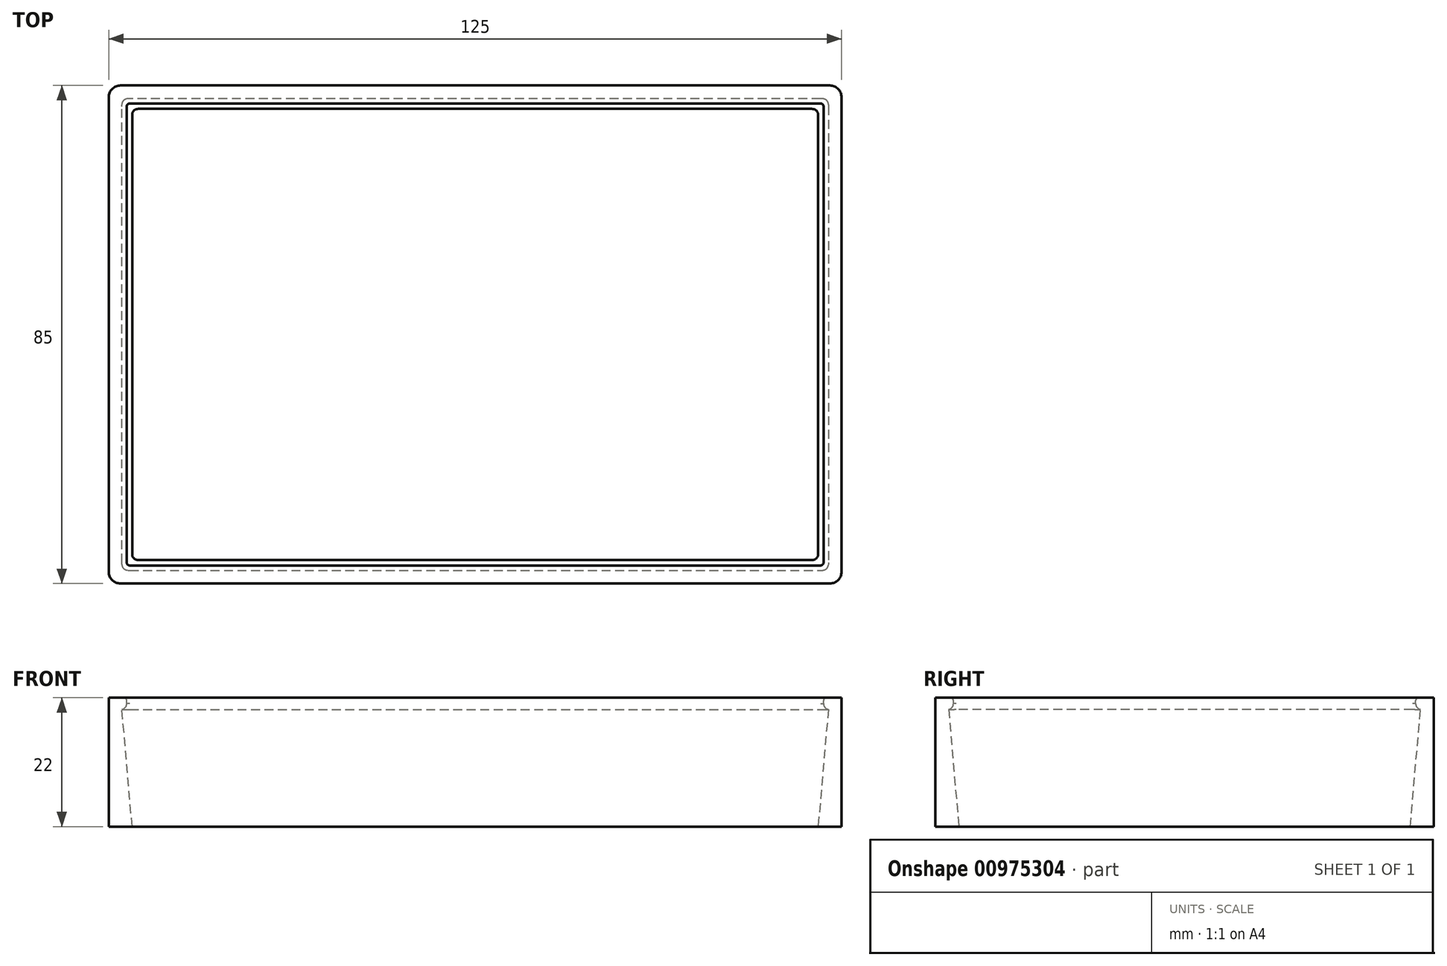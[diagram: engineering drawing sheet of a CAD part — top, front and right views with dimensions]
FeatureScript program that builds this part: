
annotation { "Feature Type Name" : "Feature", "Feature Type Description" : "" }
export const myFeature = defineFeature(function(context is Context, id is Id, definition is map)
    precondition{}
    {
        {
            var Q0;
            Q0=qCreatedBy(makeId("Top.planeOp"),FACE);
            var sketch = newSketch(context, id + "F0", { "sketchPlane" : qUnion([Q0])});
            skLineSegment(sketch, "E0.bottom", {"start": v(-62.5, 42.5) * mm, "end": v(62.5, 42.5) * mm});
            skLineSegment(sketch, "E0.top", {"start": v(-62.5, -42.5) * mm, "end": v(62.5, -42.5) * mm});
            skLineSegment(sketch, "E0.left", {"start": v(-62.5, 42.5) * mm, "end": v(-62.5, -42.5) * mm});
            skLineSegment(sketch, "E0.right", {"start": v(62.5, 42.5) * mm, "end": v(62.5, -42.5) * mm});
            skLineSegment(sketch, "E1.bottom", {"start": v(-58.5, 38.5) * mm, "end": v(58.5, 38.5) * mm});
            skLineSegment(sketch, "E1.top", {"start": v(-58.5, -38.5) * mm, "end": v(58.5, -38.5) * mm});
            skLineSegment(sketch, "E1.left", {"start": v(-58.5, 38.5) * mm, "end": v(-58.5, -38.5) * mm});
            skLineSegment(sketch, "E1.right", {"start": v(58.5, 38.5) * mm, "end": v(58.5, -38.5) * mm});
            skSolve(sketch);
        }
        {
            var Q0;
            Q0 = qSketchRegion(id + "F0", true);
            extrude(context, id + "F1", {"entities" : qUnion([Q0]), "depth" : 22 * mm, "offsetDistance" : 25 * mm});
        }
        {
            var Q0;
            Q0=qCreatedBy(makeId("Front.planeOp"),FACE);
            var sketch = newSketch(context, id + "F2", { "sketchPlane" : qUnion([Q0])});
            skLineSegment(sketch, "E2", {"start": v(-60.42, 22) * mm, "end": v(-58.5, 0) * mm});
            skLineSegment(sketch, "E3", {"start": v(-58.5, 0) * mm, "end": v(58.5, 0) * mm});
            skLineSegment(sketch, "E4", {"start": v(58.5, 0) * mm, "end": v(60.42, 22) * mm});
            skLineSegment(sketch, "E5", {"start": v(60.42, 22) * mm, "end": v(-60.42, 22) * mm});
            skSolve(sketch);
        }
        {
            var Q0;
            Q0=makeQuery(id+"F2.imprint","IMPRINT",FACE,{"disambiguationData":[TD([[makeQuery(id+"F2.imprint","IMPRINT",EDGE,{"derivedFrom":sQuery(id+"F2.wireOp",EDGE,"E2")}),1.0]])]});
            var Q1;
            Q1=makeQuery(id+"F1.opExtrude","SWEPT_FACE",FACE,{"disambiguationData":[OSD([sQuery(id+"F0.wireOp",EDGE,"E1.bottom")])]});
            var Q2;
            Q2=makeQuery(id+"F1.opExtrude","SWEPT_FACE",FACE,{"disambiguationData":[OSD([sQuery(id+"F0.wireOp",EDGE,"E1.top")])]});
            extrude(context, id + "F3", {"entities" : qUnion([Q0]), "operationType" : NewBodyOperationType.REMOVE, "endBound" : BoundingType.UP_TO_SURFACE, "oppositeDirection" : true, "depth" : 25 * mm, "endBoundEntityFace" : qUnion([Q1]), "offsetDistance" : 25 * mm, "hasSecondDirection" : true, "secondDirectionBound" : SecondDirectionBoundingType.UP_TO_SURFACE, "secondDirectionOppositeDirection" : false, "secondDirectionDepth" : 25 * mm, "secondDirectionBoundEntityFace" : qUnion([Q2])});
        }
        {
            var Q0;
            Q0=qCreatedBy(makeId("Right.planeOp"),FACE);
            var sketch = newSketch(context, id + "F4", { "sketchPlane" : qUnion([Q0])});
            skLineSegment(sketch, "E6", {"start": v(40.42, 22) * mm, "end": v(38.5, 0) * mm});
            skLineSegment(sketch, "E7", {"start": v(38.5, 0) * mm, "end": v(-38.5, 0) * mm});
            skLineSegment(sketch, "E8", {"start": v(-38.5, 0) * mm, "end": v(-40.42, 22) * mm});
            skLineSegment(sketch, "E9", {"start": v(-40.42, 22) * mm, "end": v(40.42, 22) * mm});
            skSolve(sketch);
        }
        {
            var Q0;
            Q0=makeQuery(id+"F4.imprint","IMPRINT",FACE,{"disambiguationData":[TD([[makeQuery(id+"F4.imprint","IMPRINT",EDGE,{"derivedFrom":sQuery(id+"F4.wireOp",EDGE,"E6")}),-1.0]])]});
            var Q1;
            Q1=makeQuery(id+"F3.boolean.opBoolean","COPY",FACE,{"derivedFrom":makeQuery(id+"F3.opExtrude","SWEPT_FACE",FACE,{"disambiguationData":[OSD([sQuery(id+"F2.wireOp",EDGE,"E2")])]})});
            var Q2;
            Q2=makeQuery(id+"F3.boolean.opBoolean","COPY",FACE,{"derivedFrom":makeQuery(id+"F3.opExtrude","SWEPT_FACE",FACE,{"disambiguationData":[OSD([sQuery(id+"F2.wireOp",EDGE,"E4")])]})});
            extrude(context, id + "F5", {"entities" : qUnion([Q0]), "operationType" : NewBodyOperationType.REMOVE, "endBound" : BoundingType.UP_TO_SURFACE, "oppositeDirection" : true, "depth" : 25 * mm, "endBoundEntityFace" : qUnion([Q1]), "offsetDistance" : 25 * mm, "hasSecondDirection" : true, "secondDirectionBound" : SecondDirectionBoundingType.UP_TO_SURFACE, "secondDirectionOppositeDirection" : false, "secondDirectionDepth" : 25 * mm, "secondDirectionBoundEntityFace" : qUnion([Q2])});
        }
        {
            var Q0;
            Q0=makeQuery(id+"F1.opExtrude","CAP_FACE",FACE,{"disambiguationData":[OSD([sQuery(id+"F0.wireOp",EDGE,"E0.bottom"),sQuery(id+"F0.wireOp",EDGE,"E0.top"),sQuery(id+"F0.wireOp",EDGE,"E0.left"),sQuery(id+"F0.wireOp",EDGE,"E0.right"),sQuery(id+"F0.wireOp",EDGE,"E1.bottom"),sQuery(id+"F0.wireOp",EDGE,"E1.top"),sQuery(id+"F0.wireOp",EDGE,"E1.left"),sQuery(id+"F0.wireOp",EDGE,"E1.right")])],"isStart":false});
            var sketch = newSketch(context, id + "F6", { "sketchPlane" : qUnion([Q0])});
            skLineSegment(sketch, "E10", {"start": v(-60.42, 40.42) * mm, "end": v(60.42, 40.42) * mm});
            skLineSegment(sketch, "E11", {"start": v(60.42, 40.42) * mm, "end": v(60.42, -40.42) * mm});
            skLineSegment(sketch, "E12", {"start": v(60.42, -40.42) * mm, "end": v(-60.42, -40.42) * mm});
            skLineSegment(sketch, "E13", {"start": v(-60.42, -40.42) * mm, "end": v(-60.42, 40.42) * mm});
            skLineSegment(sketch, "E14", {"start": v(-59.42, 39.42) * mm, "end": v(-59.42, -39.42) * mm});
            skLineSegment(sketch, "E15", {"start": v(-59.42, -39.42) * mm, "end": v(59.42, -39.42) * mm});
            skLineSegment(sketch, "E16", {"start": v(59.42, -39.42) * mm, "end": v(59.42, 39.42) * mm});
            skLineSegment(sketch, "E17", {"start": v(59.42, 39.42) * mm, "end": v(-59.42, 39.42) * mm});
            skSolve(sketch);
        }
        {
            var Q0;
            Q0=makeQuery(id+"F6.imprint","IMPRINT",FACE,{"disambiguationData":[TD([[makeQuery(id+"F6.imprint","IMPRINT",EDGE,{"derivedFrom":sQuery(id+"F6.wireOp",EDGE,"E10")}),-1.0]])]});
            extrude(context, id + "F7", {"entities" : qUnion([Q0]), "operationType" : NewBodyOperationType.ADD, "oppositeDirection" : true, "depth" : 2 * mm, "offsetDistance" : 25 * mm});
        }
        {
            var Q0;
            Q0=makeQuery(id+"F5.boolean.opBoolean","COPY",EDGE,{"derivedFrom":makeQuery(id+"F5.opExtrude","CAP_EDGE",EDGE,{"disambiguationData":[OSD([sQuery(id+"F4.wireOp",EDGE,"E6")]),topologyDisambiguationEdgeConnected([makeQuery(id+"F3.boolean.opBoolean","COPY",FACE,{"derivedFrom":makeQuery(id+"F3.opExtrude","SWEPT_FACE",FACE,{"disambiguationData":[OSD([sQuery(id+"F2.wireOp",EDGE,"E2")])]})})])],"isStart":false})});
            var Q1;
            Q1=makeQuery(id+"F5.boolean.opBoolean","COPY",EDGE,{"derivedFrom":makeQuery(id+"F5.opExtrude","CAP_EDGE",EDGE,{"disambiguationData":[OSD([sQuery(id+"F4.wireOp",EDGE,"E8")]),topologyDisambiguationEdgeConnected([makeQuery(id+"F3.boolean.opBoolean","COPY",FACE,{"derivedFrom":makeQuery(id+"F3.opExtrude","SWEPT_FACE",FACE,{"disambiguationData":[OSD([sQuery(id+"F2.wireOp",EDGE,"E2")])]})})])],"isStart":false})});
            var Q2;
            Q2=makeQuery(id+"F5.boolean.opBoolean","COPY",EDGE,{"derivedFrom":makeQuery(id+"F5.opExtrude","CAP_EDGE",EDGE,{"disambiguationData":[OSD([sQuery(id+"F4.wireOp",EDGE,"E6")]),topologyDisambiguationEdgeConnected([makeQuery(id+"F3.boolean.opBoolean","COPY",FACE,{"derivedFrom":makeQuery(id+"F3.opExtrude","SWEPT_FACE",FACE,{"disambiguationData":[OSD([sQuery(id+"F2.wireOp",EDGE,"E4")])]})})])],"isStart":false})});
            var Q3;
            Q3=makeQuery(id+"F5.boolean.opBoolean","COPY",EDGE,{"derivedFrom":makeQuery(id+"F5.opExtrude","CAP_EDGE",EDGE,{"disambiguationData":[OSD([sQuery(id+"F4.wireOp",EDGE,"E8")]),topologyDisambiguationEdgeConnected([makeQuery(id+"F3.boolean.opBoolean","COPY",FACE,{"derivedFrom":makeQuery(id+"F3.opExtrude","SWEPT_FACE",FACE,{"disambiguationData":[OSD([sQuery(id+"F2.wireOp",EDGE,"E4")])]})})])],"isStart":false})});
            fillet(context, id + "F8", {"entities" : qUnion([Q0, Q1, Q2, Q3]), "radius" : 1 * mm, "tangentPropagation" : true, "allowEdgeOverflow" : false});
        }
        {
            var Q0;
            Q0=makeQuery(id+"F1.opExtrude","SWEPT_EDGE",EDGE,{"disambiguationData":[OSD([sQuery(id+"F0.wireOp",EDGE,"E0.bottom"),sQuery(id+"F0.wireOp",EDGE,"E0.left")])]});
            var Q1;
            Q1=makeQuery(id+"F1.opExtrude","SWEPT_EDGE",EDGE,{"disambiguationData":[OSD([sQuery(id+"F0.wireOp",EDGE,"E0.top"),sQuery(id+"F0.wireOp",EDGE,"E0.left")])]});
            var Q2;
            Q2=makeQuery(id+"F1.opExtrude","SWEPT_EDGE",EDGE,{"disambiguationData":[OSD([sQuery(id+"F0.wireOp",EDGE,"E0.top"),sQuery(id+"F0.wireOp",EDGE,"E0.right")])]});
            var Q3;
            Q3=makeQuery(id+"F1.opExtrude","SWEPT_EDGE",EDGE,{"disambiguationData":[OSD([sQuery(id+"F0.wireOp",EDGE,"E0.bottom"),sQuery(id+"F0.wireOp",EDGE,"E0.right")])]});
            fillet(context, id + "F9", {"entities" : qUnion([Q0, Q1, Q2, Q3]), "radius" : 2 * mm, "tangentPropagation" : true, "allowEdgeOverflow" : false});
        }
        {
            var Q0;
            Q0=makeQuery(id+"F7.opExtrude","SWEPT_EDGE",EDGE,{"disambiguationData":[OSD([sQuery(id+"F6.wireOp",EDGE,"E14"),sQuery(id+"F6.wireOp",EDGE,"E17")])]});
            var Q1;
            Q1=makeQuery(id+"F7.opExtrude","SWEPT_EDGE",EDGE,{"disambiguationData":[OSD([sQuery(id+"F6.wireOp",EDGE,"E14"),sQuery(id+"F6.wireOp",EDGE,"E15")])]});
            var Q2;
            Q2=makeQuery(id+"F7.opExtrude","SWEPT_EDGE",EDGE,{"disambiguationData":[OSD([sQuery(id+"F6.wireOp",EDGE,"E15"),sQuery(id+"F6.wireOp",EDGE,"E16")])]});
            var Q3;
            Q3=makeQuery(id+"F7.opExtrude","SWEPT_EDGE",EDGE,{"disambiguationData":[OSD([sQuery(id+"F6.wireOp",EDGE,"E16"),sQuery(id+"F6.wireOp",EDGE,"E17")])]});
            fillet(context, id + "F10", {"entities" : qUnion([Q0, Q1, Q2, Q3]), "radius" : 0.5 * mm, "tangentPropagation" : true, "allowEdgeOverflow" : false});
        }
        {
            var Q0;
            Q0=makeQuery(id+"F7.opExtrude","CAP_EDGE",EDGE,{"disambiguationData":[OSD([sQuery(id+"F6.wireOp",EDGE,"E17")])],"isStart":false});
            fillet(context, id + "F11", {"entities" : qUnion([Q0]), "radius" : 1 * mm, "tangentPropagation" : true, "allowEdgeOverflow" : false});
        }
        {
            var Q0;
            Q0=makeQuery(id+"F7.opExtrude","CAP_EDGE",EDGE,{"disambiguationData":[OSD([sQuery(id+"F6.wireOp",EDGE,"E14")])],"isStart":true});
            fillet(context, id + "F12", {"entities" : qUnion([Q0]), "radius" : 0.5 * mm, "tangentPropagation" : true, "allowEdgeOverflow" : false});
        }
    });
